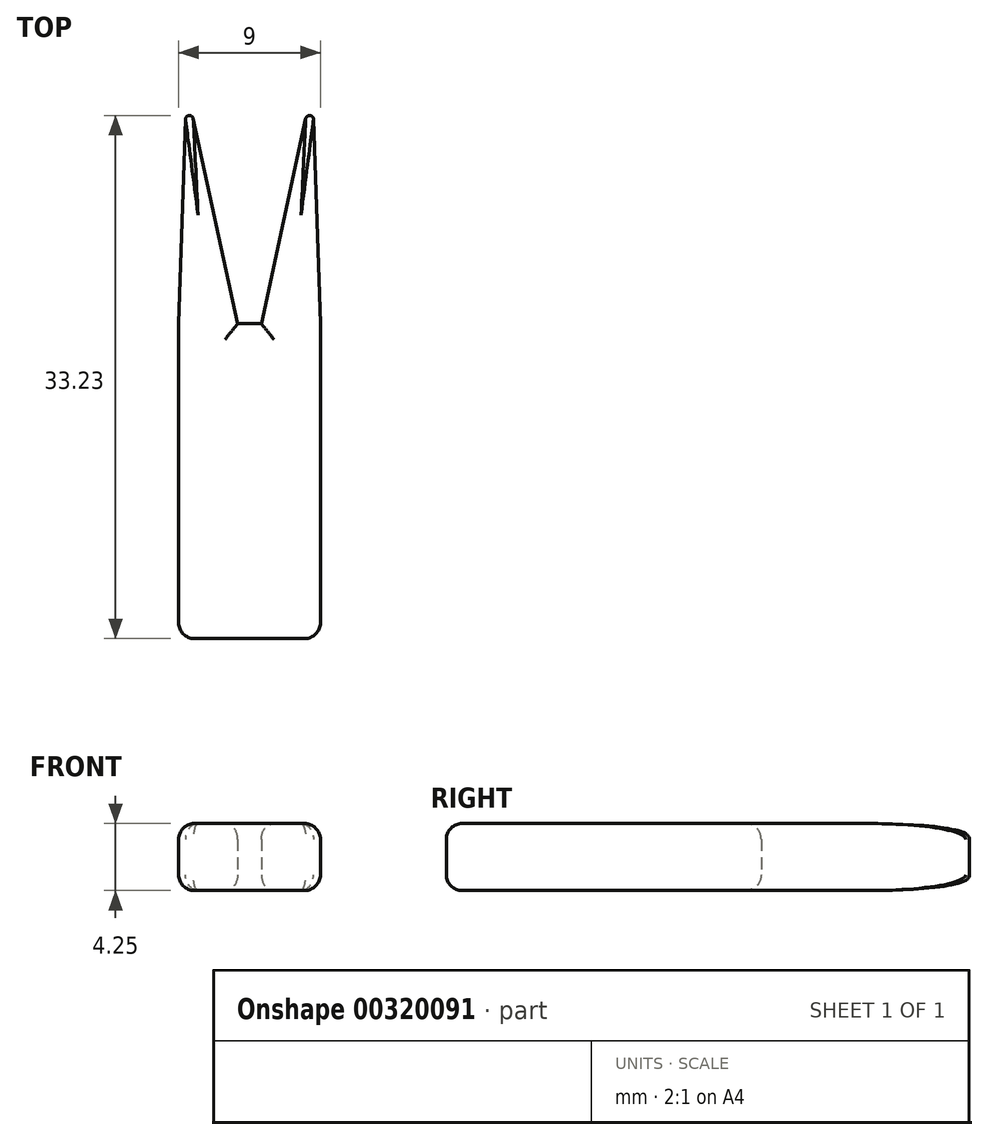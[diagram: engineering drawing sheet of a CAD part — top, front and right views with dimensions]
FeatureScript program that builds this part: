
annotation { "Feature Type Name" : "Feature", "Feature Type Description" : "" }
export const myFeature = defineFeature(function(context is Context, id is Id, definition is map)
    precondition{}
    {
        {
            var Q0;
            Q0=qCreatedBy(makeId("Top.planeOp"),FACE);
            var sketch = newSketch(context, id + "F0", { "sketchPlane" : qUnion([Q0])});
            skLineSegment(sketch, "E0.bottom", {"start": v(4.5, 10) * mm, "end": v(-4.5, 10) * mm});
            skLineSegment(sketch, "E0.top", {"start": v(4.5, -10) * mm, "end": v(-4.5, -10) * mm});
            skLineSegment(sketch, "E0.left", {"start": v(4.5, 10) * mm, "end": v(4.5, -10) * mm});
            skLineSegment(sketch, "E0.right", {"start": v(-4.5, 10) * mm, "end": v(-4.5, -10) * mm});
            skPoint(sketch, "E0.middle", {"position": v(0, 0) * mm});
            skLineSegment(sketch, "E1", {"start": v(-0.75, 10) * mm, "end": v(-4, 25) * mm});
            skLineSegment(sketch, "E2.MirrorCS", {"start": v(0.75, 10) * mm, "end": v(4, 25) * mm});
            skLineSegment(sketch, "E3", {"start": v(-4, 25) * mm, "end": v(-4.5, 10) * mm});
            skLineSegment(sketch, "E4.MirrorCS", {"start": v(4, 25) * mm, "end": v(4.5, 10) * mm});
            skPoint(sketch, "E5", {"position": v(-3.25, 21.54) * mm});
            skPoint(sketch, "E6.MirrorP", {"position": v(3.25, 21.54) * mm});
            skSolve(sketch);
        }
        {
            var Q0;
            Q0=makeQuery(id+"F0.imprint","IMPRINT",FACE,{"disambiguationData":[TD([[makeQuery(id+"F0.imprint","IMPRINT",EDGE,{"derivedFrom":sQuery(id+"F0.wireOp",EDGE,"E0.top")}),-1.0]])]});
            var Q1;
            {var subQ2=sQuery(id+"F0.wireOp",EDGE,"E1");Q1=makeQuery(id+"F0.imprint","IMPRINT",FACE,{"disambiguationData":[TD([[makeQuery(id+"F0.imprint","IMPRINT",EDGE,{"derivedFrom":subQ2}),1.0]])]});}
            var Q2;
            {var subQ2=sQuery(id+"F0.wireOp",EDGE,"E2.MirrorCS");Q2=makeQuery(id+"F0.imprint","IMPRINT",FACE,{"disambiguationData":[TD([[makeQuery(id+"F0.imprint","IMPRINT",EDGE,{"derivedFrom":subQ2}),-1.0]])]});}
            extrude(context, id + "F1", {"entities" : qUnion([Q0, Q1, Q2]), "depth" : 4.25 * mm});
        }
        {
            var Q0;
            Q0=makeQuery(id+"F1.opExtrude","CAP_FACE",FACE,{"disambiguationData":[OSD([sQuery(id+"F0.wireOp",EDGE,"E0.bottom"),sQuery(id+"F0.wireOp",EDGE,"E0.top"),sQuery(id+"F0.wireOp",EDGE,"E0.left"),sQuery(id+"F0.wireOp",EDGE,"E0.right"),sQuery(id+"F0.wireOp",EDGE,"E1"),sQuery(id+"F0.wireOp",EDGE,"E2.MirrorCS"),sQuery(id+"F0.wireOp",EDGE,"E3"),sQuery(id+"F0.wireOp",EDGE,"E4.MirrorCS")])],"isStart":false});
            var Q1;
            Q1=makeQuery(id+"F1.opExtrude","CAP_FACE",FACE,{"disambiguationData":[OSD([sQuery(id+"F0.wireOp",EDGE,"E0.bottom"),sQuery(id+"F0.wireOp",EDGE,"E0.top"),sQuery(id+"F0.wireOp",EDGE,"E0.left"),sQuery(id+"F0.wireOp",EDGE,"E0.right"),sQuery(id+"F0.wireOp",EDGE,"E1"),sQuery(id+"F0.wireOp",EDGE,"E2.MirrorCS"),sQuery(id+"F0.wireOp",EDGE,"E3"),sQuery(id+"F0.wireOp",EDGE,"E4.MirrorCS")])],"isStart":true});
            var Q2;
            Q2=makeQuery(id+"F1.opExtrude","SWEPT_FACE",FACE,{"disambiguationData":[OSD([sQuery(id+"F0.wireOp",EDGE,"E0.left")])]});
            var Q3;
            Q3=makeQuery(id+"F1.opExtrude","SWEPT_FACE",FACE,{"disambiguationData":[OSD([sQuery(id+"F0.wireOp",EDGE,"E0.right")])]});
            fillet(context, id + "F2", {"entities" : qUnion([Q0, Q1, Q2, Q3]), "radius" : 1 * mm, "tangentPropagation" : true, "allowEdgeOverflow" : false});
        }
        {
            var Q0;
            Q0=makeQuery(id+"F1.opExtrude","SWEPT_EDGE",EDGE,{"disambiguationData":[OSD([sQuery(id+"F0.wireOp",EDGE,"E2.MirrorCS"),sQuery(id+"F0.wireOp",EDGE,"E4.MirrorCS")])]});
            var Q1;
            Q1=makeQuery(id+"F1.opExtrude","SWEPT_EDGE",EDGE,{"disambiguationData":[OSD([sQuery(id+"F0.wireOp",EDGE,"E1"),sQuery(id+"F0.wireOp",EDGE,"E3")])]});
            fillet(context, id + "F3", {"entities" : qUnion([Q0, Q1]), "radius" : .25 * mm, "tangentPropagation" : true, "allowEdgeOverflow" : false});
        }
    });
